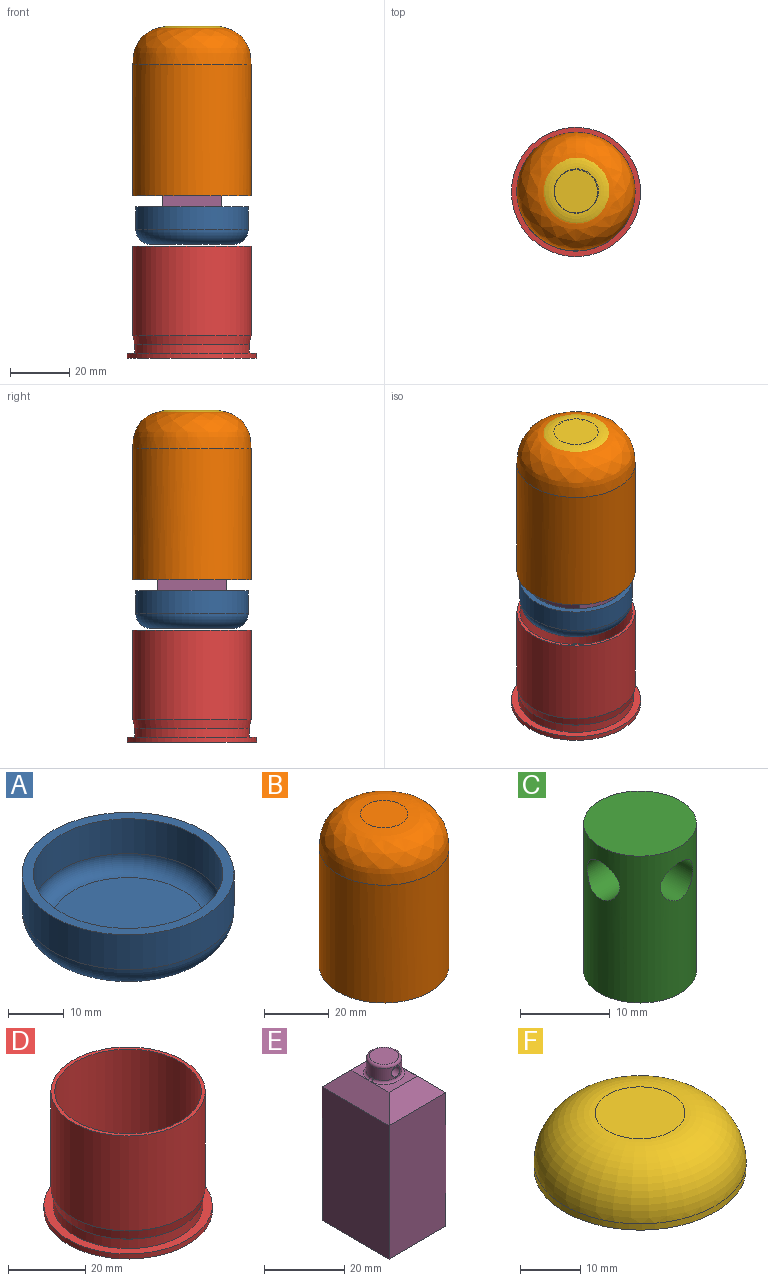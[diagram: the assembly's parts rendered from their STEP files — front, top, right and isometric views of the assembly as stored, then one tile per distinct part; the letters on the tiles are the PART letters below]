
ASSEMBLY  parts=6 mates=5
PART A: 7 faces, bbox 41.1x41.1x12.7 mm
  f0: cylinder r=18.99mm len=37.99mm, axis (0,0,-1), area 909.3mm2, adj f1,f3
  f1: plane 37.99x37.99mm, normal (0,0,1), area 226.1mm2, adj f0,f4
  f2: plane 27.83x27.83mm, normal (0,0,-1), area 608.1mm2, adj f3
  f3: torus R=13.91mm, axis (0,0,1), area 859.7mm2, adj f0,f2
  f4: cylinder r=16.99mm len=33.99mm, axis (0,0,-1), area 813.6mm2, adj f1,f6
  f5: plane 27.83x27.83mm, normal (0,0,1), area 608.1mm2, adj f6
  f6: torus R=13.91mm, axis (0,0,1), area 482.5mm2, adj f4,f5
PART B: 7 faces, bbox 44x44x61.2 mm
  f0: cylinder r=20mm len=44.45mm, axis (0,0,-1), area 5585.8mm2, adj f2,f3
  f1: plane 14.61x14.61mm, normal (0,0,1), area 167.4mm2, adj f3
  f2: plane 40x40mm, normal (0,0,-1), area 239.5mm2, adj f0,f4
  f3: bspline ~40x40mm, area 2028.7mm2, adj f0,f1
  f4: cylinder r=17.99mm len=44.45mm, axis (0,0,-1), area 5025.3mm2, adj f2,f6
  f5: plane 14.6x14.6mm, normal (0,0,-1), area 167.4mm2, adj f6
  f6: offset ~44.01x44.01mm, area 1577.8mm2, adj f4,f5
PART C: 9 faces, bbox 12.6x12.6x20.1 mm
  f0: cylinder r=6.3mm len=20.07mm, axis (0,0,-1), area 711.4mm2, adj f1,f2,f5,f6,f7,f8
  f1: cylinder r=2.54mm len=6.3mm, axis (0,1,0), area 70.5mm2, adj f0,f3,f4,f7,f8
  f2: cylinder r=2.54mm len=6.3mm, axis (0,-1,0), area 70.5mm2, adj f0,f3,f4,f7,f8
  f3: plane 1.45x0.13mm, normal (0,1,0), area 0.1mm2, adj f1,f2,f7,f8
  f4: plane 1.44x0.13mm, normal (1,0,0), area 0.1mm2, adj f1,f2,f7,f8
  f5: plane 12.6x12.6mm, normal (0,0,1), area 124.7mm2, adj f0
  f6: plane 12.6x12.6mm, normal (0,0,-1), area 124.7mm2, adj f0
  f7: cylinder r=2.54mm len=6.3mm, axis (-1,0,0), area 70.6mm2, adj f0,f1,f2,f3,f4
  f8: cylinder r=2.54mm len=6.3mm, axis (1,0,0), area 70.5mm2, adj f0,f1,f2,f3,f4
PART D: 15 faces, bbox 43.7x43.7x37.7 mm
  f0: cylinder r=21.83mm len=43.66mm, axis (0,0,-1), area 217.8mm2, adj f1,f2
  f1: plane 43.66x43.66mm, normal (0,0,1), area 317.4mm2, adj f0,f3
  f2: plane 43.66x43.66mm, normal (0,0,-1), area 1370.6mm2, adj f0,f14
  f3: cylinder r=19.38mm len=38.76mm, axis (0,0,-1), area 365.3mm2, adj f1,f5
  f4: cone r=19.41mm half-angle=10deg, axis (0,0,1), area 376.7mm2, adj f5,f8
  f5: plane 38.83x38.83mm, normal (0,0,-1), area 4.3mm2, adj f3,f4
  f6: cylinder r=20mm len=40mm, axis (0,0,-1), area 3788.7mm2, adj f7,f8
  f7: plane 40x40mm, normal (0,0,1), area 122.5mm2, adj f6,f13
  f8: plane 40x40mm, normal (0,0,-1), area 7.1mm2, adj f4,f6
  f9: plane 36.76x36.76mm, normal (0,0,1), area 934.6mm2, adj f10,f14
  f10: cylinder r=18.38mm len=36.76mm, axis (0,0,-1), area 529.8mm2, adj f9,f12
  f11: cone r=18.43mm half-angle=10deg, axis (0,0,1), area 288.8mm2, adj f12,f13
  f12: plane 37.15x37.15mm, normal (0,0,1), area 22.7mm2, adj f10,f11
  f13: cylinder r=19mm len=38mm, axis (0,0,-1), area 3550.4mm2, adj f7,f11
  f14: cylinder r=6.35mm len=12.7mm, axis (0,0,-1), area 39.9mm2, adj f2,f9
PART E: 19 faces, bbox 20.1x23.6x50.8 mm
  f0: cylinder r=4.38mm len=8.76mm, axis (0,0,-1), area 84.5mm2, adj f13,f14,f15,f16,f17,f18
  f1: plane 9.88x6.16mm, normal (0,0,1), area 26.7mm2, adj f8,f10,f11,f14
  f2: plane 40.64x20.04mm, normal (0,1,0), area 814.3mm2, adj f3,f5,f7,f9
  f3: plane 40.64x23.56mm, normal (-1,0,0), area 957.3mm2, adj f2,f4,f7,f8
  f4: plane 40.64x20.04mm, normal (0,-1,0), area 814.3mm2, adj f3,f5,f7,f10
  f5: plane 40.64x23.56mm, normal (1,0,0), area 957.3mm2, adj f2,f4,f7,f11
  f6: plane 9.88x5.89mm, normal (0,0,1), area 24.1mm2, adj f8,f9,f11,f15
  f7: plane 23.56x20.04mm, normal (0,0,-1), area 472mm2, adj f2,f3,f4,f5
  f8: plane 23.56x5.08mm, normal (-0.71,0,0.71), area 132.7mm2, adj f1,f3,f6,f9,f10,f13
  f9: plane 20.04x5.08mm, normal (0,0.71,0.71), area 107.4mm2, adj f2,f6,f8,f11
  f10: plane 20.04x5.08mm, normal (0,-0.71,0.71), area 107.4mm2, adj f1,f4,f8,f11
  f11: plane 23.59x5.11mm, normal (0.71,0,0.71), area 132.7mm2, adj f1,f5,f6,f9,f10,f16
  f12: plane 7.29x7.29mm, normal (0,0,1), area 41.8mm2, adj f17
  f13: bspline ~1.85x0.77mm, area 1.4mm2, adj f0,f8,f14,f15
  f14: torus R=5.12mm, axis (0,0,1), area 14.3mm2, adj f0,f1,f13,f16
  f15: torus R=5.12mm, axis (0,0,1), area 14.3mm2, adj f0,f6,f13,f16
  f16: bspline ~4.07x0.89mm, area 3mm2, adj f0,f11,f14,f15
  f17: torus R=3.65mm, axis (0,0,1), area 29.9mm2, adj f0,f12
  f18: cylinder r=1.52mm len=8.76mm, axis (0,1,0), area 81.3mm2, adj f0
PART F: 4 faces, bbox 35.3x35.3x11.4 mm
  f0: cylinder r=17.64mm len=35.28mm, axis (0,0,-1), area 140.8mm2, adj f2,f3
  f1: plane 14.96x14.96mm, normal (0,0,1), area 175.8mm2, adj f3
  f2: plane 35.28x35.28mm, normal (0,0,-1), area 977.6mm2, adj f0
  f3: torus R=7.48mm, axis (0,0,1), area 1398.7mm2, adj f0,f1
PLACE A t=(1.5,0.89,16.14)mm
PLACE B rot(axis=(0,0,1),90deg) t=(1.5,0.89,26.18)mm
PLACE C t=(1.5,0.89,-28.59)mm
PLACE D t=(1.5,0.89,-28.59)mm
PLACE E t=(1.64,1.03,15.99)mm
PLACE F t=(1.64,1.03,72.22)mm
MATE slider B.f0 <-> A.f0  axis (0,0,-1) through (1.5,0.89,26.18)mm
MATE slider B.f0 <-> D.f6  axis (0,0,-1) through (1.5,0.89,26.18)mm
MATE fastened C.f0 <-> D.f14  axis (0,0,-1) through (1.5,0.89,-28.59)mm
MATE slider F.f0 <-> E.f0  axis (0,0,-1) through (1.64,1.03,72.22)mm
MATE slider E.f7 <-> A.f0  axis (0,0,-1) through (1.5,0.89,15.99)mm
